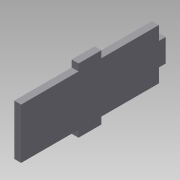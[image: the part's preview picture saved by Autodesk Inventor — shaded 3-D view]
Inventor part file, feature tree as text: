
AUTODESK INVENTOR PART (.ipt)
format: ipt  version: 2013 (Build 170138000, 138)  size: 90,624 bytes
history: native  units: mm
features: extrude x1, sketch x1
ambient origin geometry x8: Origin, YZ Plane, XZ Plane, XY Plane, X Axis, Y Axis, Z Axis, Center Point
bodies: Solid1 (feature_tree)
feature tree (2):
  extrude  "Extrusion1"  Depth=10.0mm
  sketch  "Sketch1"  dims[d2=3.0mm d3=10.0mm d4=28.0mm d5=3.0mm d6=3.0mm d7=28.0mm d11=3.0mm d12=10.0mm d17=3.0mm d18=0.0mm d19=22.0mm d23=6.0mm d24=10.0mm d25=6.0mm d26=25.0mm d27=25.0mm d28=25.0mm d29=10.0mm d30=25.0mm]
